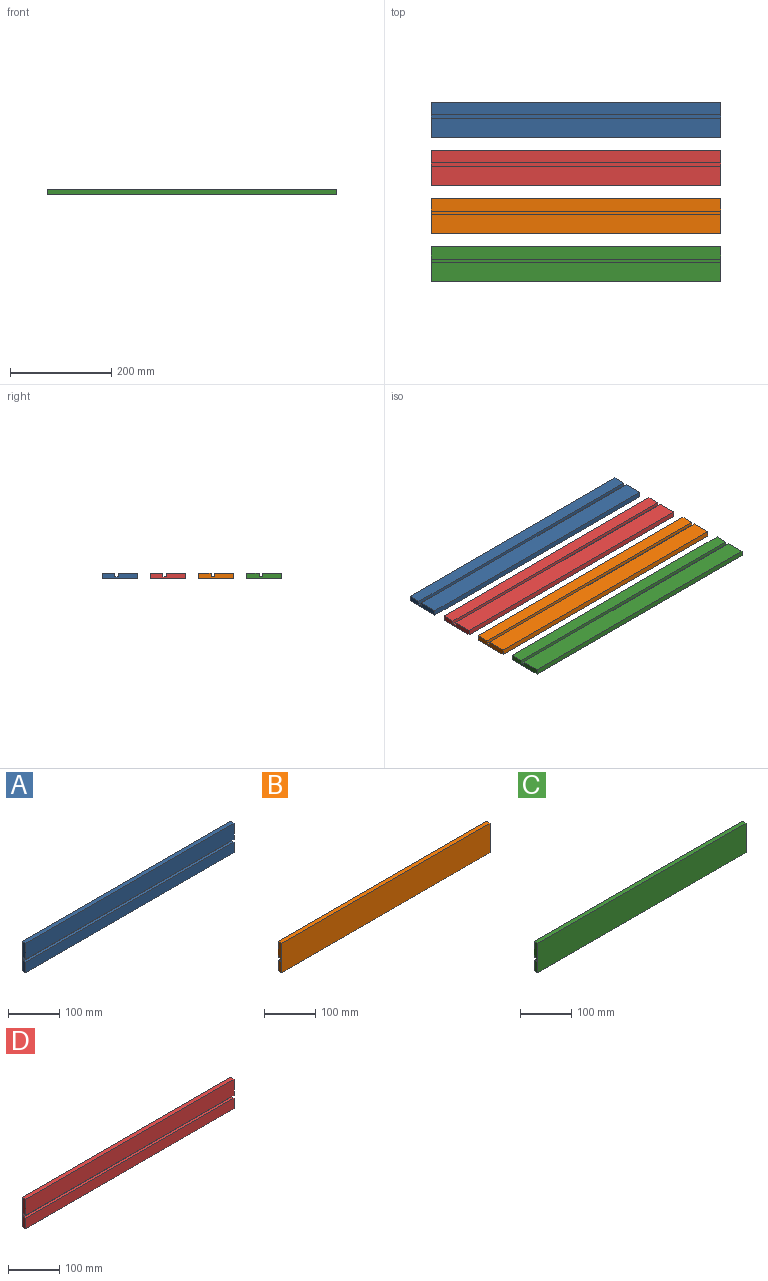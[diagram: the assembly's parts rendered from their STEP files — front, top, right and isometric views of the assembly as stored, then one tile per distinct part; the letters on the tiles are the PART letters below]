
ASSEMBLY  parts=4 mates=3
PART A: 10 faces, bbox 573.4x10.8x69.9 mm
  f0: plane 573.41x37.72mm, normal (0,-1,0), area 21628.3mm2, adj f1,f2,f4,f9
  f1: plane 69.85x10.8mm, normal (1,0,0), area 706.2mm2, adj f0,f3,f4,f5,f6,f7,f8,f9
  f2: plane 69.85x10.8mm, normal (-1,0,0), area 706.2mm2, adj f0,f3,f4,f5,f6,f7,f8,f9
  f3: plane 573.41x25.02mm, normal (0,-1,0), area 14346mm2, adj f1,f2,f6,f8
  f4: plane 573.41x10.8mm, normal (0,0,1), area 6189.9mm2, adj f0,f1,f2,f5
  f5: plane 573.41x69.85mm, normal (0,1,0), area 40052.3mm2, adj f1,f2,f4,f6
  f6: plane 573.41x10.8mm, normal (0,0,-1), area 6189.9mm2, adj f1,f2,f3,f5
  f7: plane 573.41x7.11mm, normal (0,-1,0), area 4078.1mm2, adj f1,f2,f8,f9
  f8: plane 573.41x6.73mm, normal (0,0,1), area 3859.6mm2, adj f1,f2,f3,f7
  f9: plane 573.41x6.73mm, normal (0,0,-1), area 3859.6mm2, adj f0,f1,f2,f7
PART B: 10 faces, bbox 573.4x10.8x69.9 mm
  f0: plane 573.41x37.72mm, normal (0,1,0), area 21628.3mm2, adj f1,f2,f5,f9
  f1: plane 69.85x10.8mm, normal (-1,0,0), area 706.2mm2, adj f0,f3,f4,f5,f6,f7,f8,f9
  f2: plane 69.85x10.8mm, normal (1,0,0), area 706.2mm2, adj f0,f3,f4,f5,f6,f7,f8,f9
  f3: plane 573.41x25.02mm, normal (0,1,0), area 14346mm2, adj f1,f2,f4,f8
  f4: plane 573.41x10.8mm, normal (0,0,-1), area 6189.9mm2, adj f1,f2,f3,f6
  f5: plane 573.41x10.8mm, normal (0,0,1), area 6189.9mm2, adj f0,f1,f2,f6
  f6: plane 573.41x69.85mm, normal (0,-1,0), area 40052.3mm2, adj f1,f2,f4,f5
  f7: plane 573.41x7.11mm, normal (0,1,0), area 4078.1mm2, adj f1,f2,f8,f9
  f8: plane 573.41x6.73mm, normal (0,0,1), area 3859.6mm2, adj f1,f2,f3,f7
  f9: plane 573.41x6.73mm, normal (0,0,-1), area 3859.6mm2, adj f0,f1,f2,f7
PART C: 10 faces, bbox 573.4x10.8x69.9 mm
  f0: plane 573.41x37.72mm, normal (0,1,0), area 21628.3mm2, adj f1,f2,f5,f9
  f1: plane 69.85x10.8mm, normal (-1,0,0), area 706.2mm2, adj f0,f3,f4,f5,f6,f7,f8,f9
  f2: plane 69.85x10.8mm, normal (1,0,0), area 706.2mm2, adj f0,f3,f4,f5,f6,f7,f8,f9
  f3: plane 573.41x25.02mm, normal (0,1,0), area 14346mm2, adj f1,f2,f4,f8
  f4: plane 573.41x10.8mm, normal (0,0,-1), area 6189.9mm2, adj f1,f2,f3,f6
  f5: plane 573.41x10.8mm, normal (0,0,1), area 6189.9mm2, adj f0,f1,f2,f6
  f6: plane 573.41x69.85mm, normal (0,-1,0), area 40052.3mm2, adj f1,f2,f4,f5
  f7: plane 573.41x7.11mm, normal (0,1,0), area 4078.1mm2, adj f1,f2,f8,f9
  f8: plane 573.41x6.73mm, normal (0,0,1), area 3859.6mm2, adj f1,f2,f3,f7
  f9: plane 573.41x6.73mm, normal (0,0,-1), area 3859.6mm2, adj f0,f1,f2,f7
PART D: 10 faces, bbox 573.4x10.8x69.9 mm
  f0: plane 573.41x37.72mm, normal (0,-1,0), area 21628.3mm2, adj f1,f2,f4,f9
  f1: plane 69.85x10.8mm, normal (1,0,0), area 706.2mm2, adj f0,f3,f4,f5,f6,f7,f8,f9
  f2: plane 69.85x10.8mm, normal (-1,0,0), area 706.2mm2, adj f0,f3,f4,f5,f6,f7,f8,f9
  f3: plane 573.41x25.02mm, normal (0,-1,0), area 14346mm2, adj f1,f2,f6,f8
  f4: plane 573.41x10.8mm, normal (0,0,1), area 6189.9mm2, adj f0,f1,f2,f5
  f5: plane 573.41x69.85mm, normal (0,1,0), area 40052.3mm2, adj f1,f2,f4,f6
  f6: plane 573.41x10.8mm, normal (0,0,-1), area 6189.9mm2, adj f1,f2,f3,f5
  f7: plane 573.41x7.11mm, normal (0,-1,0), area 4078.1mm2, adj f1,f2,f8,f9
  f8: plane 573.41x6.73mm, normal (0,0,1), area 3859.6mm2, adj f1,f2,f3,f7
  f9: plane 573.41x6.73mm, normal (0,0,-1), area 3859.6mm2, adj f0,f1,f2,f7
PLACE A rot(axis=(0,-0.71,0.71),180deg) t=(21.01,-47.14,-178.23)mm
PLACE B rot(axis=(1,0,0),90deg) t=(21.01,35.41,107.52)mm
PLACE C rot(axis=(1,0,0),90deg) t=(21.01,-332.89,107.52)mm
PLACE D rot(axis=(0,-0.71,0.71),180deg) t=(21.01,130.66,-178.23)mm
MATE fastened B.f1 <-> C.f1  axis (-1,0,0) through (-265.69,-66.57,-167.81)mm
MATE fastened A.f1 <-> D.f1  axis (-1,0,0) through (-265.69,127.48,-167.81)mm
MATE fastened D.f1 <-> B.f1  axis (-1,0,0) through (-265.69,32.23,-167.81)mm
